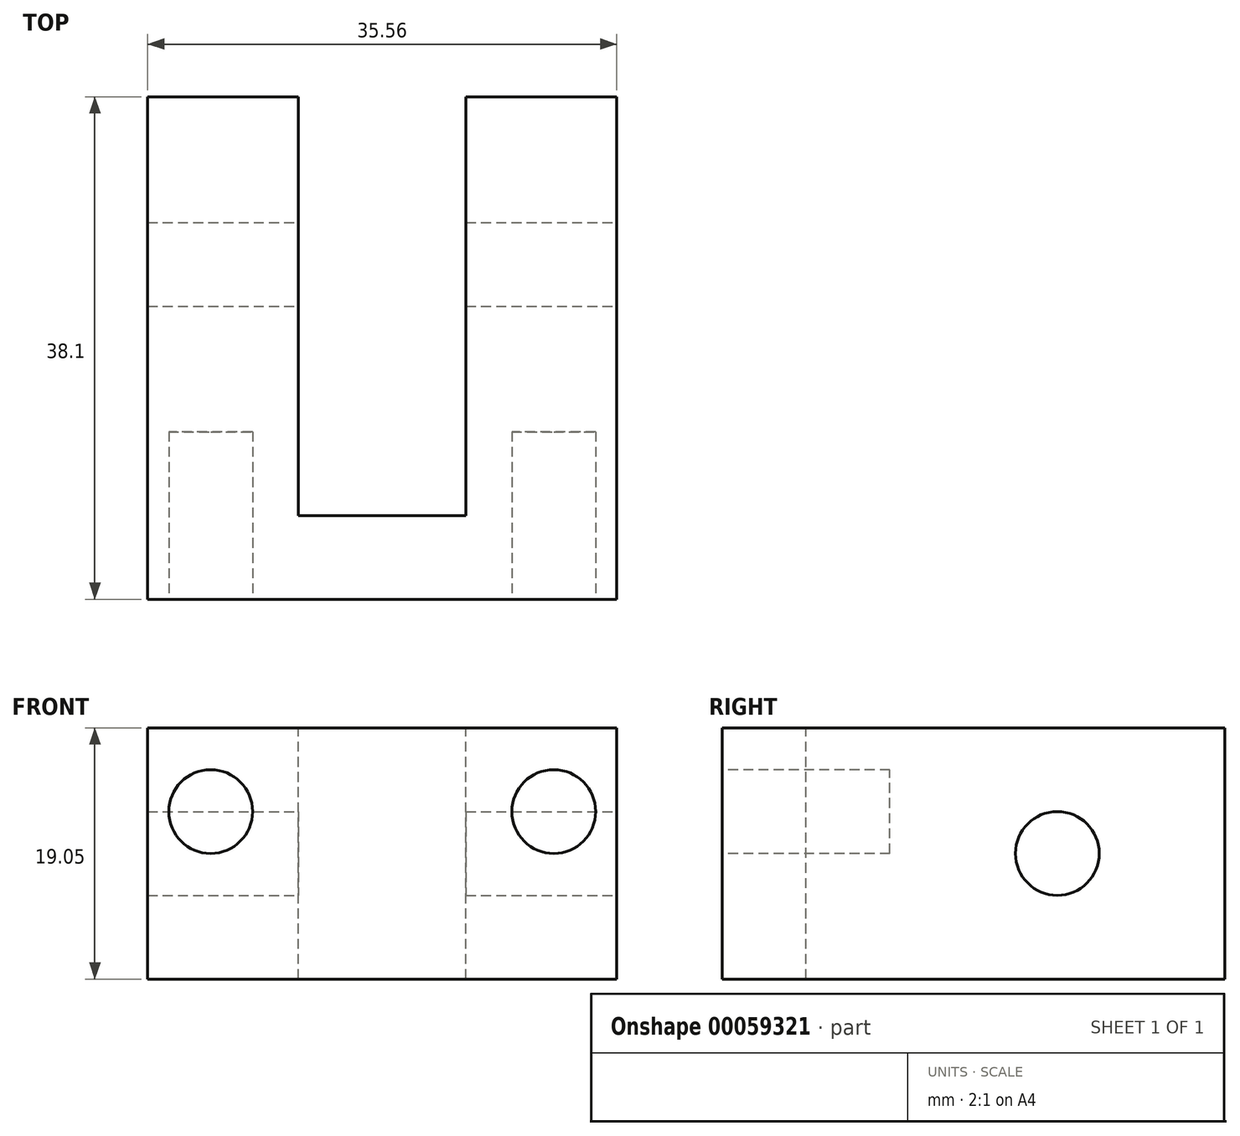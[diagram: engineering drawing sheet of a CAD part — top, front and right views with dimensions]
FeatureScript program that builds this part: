
annotation { "Feature Type Name" : "Feature", "Feature Type Description" : "" }
export const myFeature = defineFeature(function(context is Context, id is Id, definition is map)
    precondition{}
    {
        {
            var Q0;
            Q0=qCreatedBy(makeId("Top.planeOp"),FACE);
            var sketch = newSketch(context, id + "F0", { "sketchPlane" : qUnion([Q0])});
            skLineSegment(sketch, "E0.bottom", {"start": v(0, 38.1) * mm, "end": v(35.56, 38.1) * mm});
            skLineSegment(sketch, "E0.top", {"start": v(0, 0) * mm, "end": v(35.56, 0) * mm});
            skLineSegment(sketch, "E0.left", {"start": v(0, 38.1) * mm, "end": v(0, 0) * mm});
            skLineSegment(sketch, "E0.right", {"start": v(35.56, 38.1) * mm, "end": v(35.56, 0) * mm});
            skSolve(sketch);
        }
        {
            var Q0;
            Q0=makeQuery(id+"F0.imprint","IMPRINT",FACE,{"disambiguationData":[TD([[makeQuery(id+"F0.imprint","IMPRINT",EDGE,{"derivedFrom":sQuery(id+"F0.wireOp",EDGE,"E0.bottom")}),-1.0]])]});
            extrude(context, id + "F1", {"entities" : qUnion([Q0]), "depth" : 19.05 * mm});
        }
        {
            var Q0;
            Q0=makeQuery(id+"F1.opExtrude","CAP_FACE",FACE,{"disambiguationData":[OSD([sQuery(id+"F0.wireOp",EDGE,"E0.bottom"),sQuery(id+"F0.wireOp",EDGE,"E0.top"),sQuery(id+"F0.wireOp",EDGE,"E0.left"),sQuery(id+"F0.wireOp",EDGE,"E0.right")])],"isStart":false});
            var sketch = newSketch(context, id + "F2", { "sketchPlane" : qUnion([Q0])});
            skLineSegment(sketch, "E1.bottom", {"start": v(11.43, 38.1) * mm, "end": v(24.13, 38.1) * mm});
            skLineSegment(sketch, "E1.top", {"start": v(11.43, 6.35) * mm, "end": v(24.13, 6.35) * mm});
            skLineSegment(sketch, "E1.left", {"start": v(11.43, 38.1) * mm, "end": v(11.43, 6.35) * mm});
            skLineSegment(sketch, "E1.right", {"start": v(24.13, 38.1) * mm, "end": v(24.13, 6.35) * mm});
            skSolve(sketch);
        }
        {
            var Q0;
            Q0=makeQuery(id+"F2.imprint","IMPRINT",FACE,{"disambiguationData":[TD([[makeQuery(id+"F2.imprint","IMPRINT",EDGE,{"derivedFrom":sQuery(id+"F2.wireOp",EDGE,"E1.bottom")}),-1.0]])]});
            extrude(context, id + "F3", {"entities" : qUnion([Q0]), "operationType" : NewBodyOperationType.REMOVE, "oppositeDirection" : true, "depth" : 19.05 * mm});
        }
        {
            var Q0;
            Q0=makeQuery(id+"F1.opExtrude","SWEPT_FACE",FACE,{"disambiguationData":[OSD([sQuery(id+"F0.wireOp",EDGE,"E0.top")])]});
            var sketch = newSketch(context, id + "F4", { "sketchPlane" : qUnion([Q0])});
            skCircle(sketch, "E2", {"center": v(4.78, 12.7) * mm, "radius": 3.18 * mm});
            skCircle(sketch, "E3", {"center": v(30.78, 12.7) * mm, "radius": 3.18 * mm});
            skSolve(sketch);
        }
        {
            var Q0;
            Q0=makeQuery(id+"F4.imprint","IMPRINT",FACE,{"disambiguationData":[TD([[makeQuery(id+"F4.imprint","IMPRINT",EDGE,{"derivedFrom":sQuery(id+"F4.wireOp",EDGE,"E2")}),1.0]])]});
            var Q1;
            Q1=makeQuery(id+"F4.imprint","IMPRINT",FACE,{"disambiguationData":[TD([[makeQuery(id+"F4.imprint","IMPRINT",EDGE,{"derivedFrom":sQuery(id+"F4.wireOp",EDGE,"E3")}),1.0]])]});
            extrude(context, id + "F5", {"entities" : qUnion([Q0, Q1]), "operationType" : NewBodyOperationType.REMOVE, "oppositeDirection" : true, "depth" : 12.7 * mm});
        }
        {
            var Q0;
            Q0=makeQuery(id+"F1.opExtrude","SWEPT_FACE",FACE,{"disambiguationData":[OSD([sQuery(id+"F0.wireOp",EDGE,"E0.right")])]});
            var sketch = newSketch(context, id + "F6", { "sketchPlane" : qUnion([Q0])});
            skCircle(sketch, "E4", {"center": v(25.4, 9.53) * mm, "radius": 3.18 * mm});
            skSolve(sketch);
        }
        {
            var Q0;
            Q0=makeQuery(id+"F6.imprint","IMPRINT",FACE,{"disambiguationData":[TD([[makeQuery(id+"F6.imprint","IMPRINT",EDGE,{"derivedFrom":sQuery(id+"F6.wireOp",EDGE,"E4")}),1.0]])]});
            extrude(context, id + "F7", {"entities" : qUnion([Q0]), "operationType" : NewBodyOperationType.REMOVE, "oppositeDirection" : true, "depth" : 508 * mm});
        }
    });
